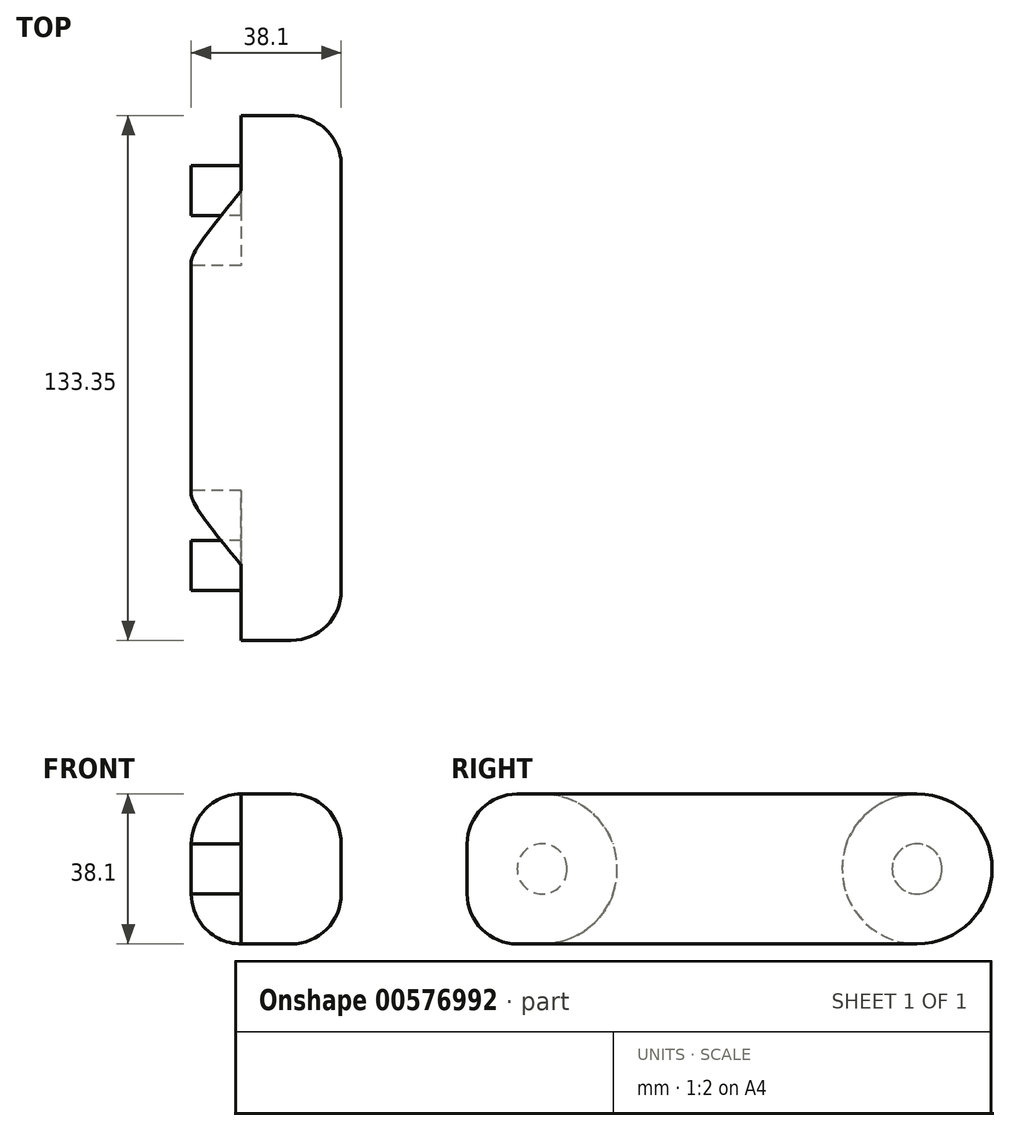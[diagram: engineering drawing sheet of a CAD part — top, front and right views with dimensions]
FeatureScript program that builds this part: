
annotation { "Feature Type Name" : "Feature", "Feature Type Description" : "" }
export const myFeature = defineFeature(function(context is Context, id is Id, definition is map)
    precondition{}
    {
        {
            var Q0;
            Q0=qCreatedBy(makeId("Right.planeOp"),FACE);
            var sketch = newSketch(context, id + "F0", { "sketchPlane" : qUnion([Q0])});
            skLineSegment(sketch, "E0.bottom", {"start": v(12.7, 0) * mm, "end": v(88.9, 0) * mm});
            skLineSegment(sketch, "E0.top", {"start": v(12.7, 38.1) * mm, "end": v(88.9, 38.1) * mm});
            skLineSegment(sketch, "E0.left", {"start": v(0, 12.7) * mm, "end": v(0, 25.4) * mm});
            skPoint(sketch, "E1.visualSharp", {"position": v(0, 38.1) * mm});
            skArc(sketch, "E1.filletArc", {"start": v(12.7, 38.1) * mm, "mid": v(3.72, 34.38) * mm, "end": v(0, 25.4) * mm});
            skPoint(sketch, "E2.visualSharp", {"position": v(101.6, 38.1) * mm});
            skPoint(sketch, "E3.visualSharp", {"position": v(101.6, 0) * mm});
            skPoint(sketch, "E4.visualSharp", {"position": v(0, 0) * mm});
            skArc(sketch, "E4.filletArc", {"start": v(0, 12.7) * mm, "mid": v(3.72, 3.72) * mm, "end": v(12.7, 0) * mm});
            skLineSegment(sketch, "E5", {"start": v(88.9, 0) * mm, "end": v(114.3, 0) * mm});
            skLineSegment(sketch, "E6", {"start": v(88.9, 38.1) * mm, "end": v(114.3, 38.1) * mm});
            skArc(sketch, "E7", {"start": v(114.3, 0) * mm, "mid": v(133.35, 19.05) * mm, "end": v(114.3, 38.1) * mm});
            skSolve(sketch);
        }
        {
            var Q0;
            Q0=makeQuery(id+"F0.imprint","IMPRINT",FACE,{"disambiguationData":[TD([[makeQuery(id+"F0.imprint","IMPRINT",EDGE,{"derivedFrom":sQuery(id+"F0.wireOp",EDGE,"E0.bottom")}),1.0]])]});
            extrude(context, id + "F1", {"entities" : qUnion([Q0]), "depth" : 38.1 * mm, "offsetDistance" : 25.4 * mm});
        }
        {
            var Q0;
            Q0=makeQuery(id+"F1.opExtrude","CAP_FACE",FACE,{"disambiguationData":[OSD([sQuery(id+"F0.wireOp",EDGE,"E0.bottom"),sQuery(id+"F0.wireOp",EDGE,"E0.top"),sQuery(id+"F0.wireOp",EDGE,"E0.left"),sQuery(id+"F0.wireOp",EDGE,"E1.filletArc"),sQuery(id+"F0.wireOp",EDGE,"E4.filletArc"),sQuery(id+"F0.wireOp",EDGE,"E5"),sQuery(id+"F0.wireOp",EDGE,"E6"),sQuery(id+"F0.wireOp",EDGE,"E7")])],"isStart":false});
            var Q1;
            Q1=makeQuery(id+"F1.opExtrude","CAP_FACE",FACE,{"disambiguationData":[OSD([sQuery(id+"F0.wireOp",EDGE,"E0.bottom"),sQuery(id+"F0.wireOp",EDGE,"E0.top"),sQuery(id+"F0.wireOp",EDGE,"E0.left"),sQuery(id+"F0.wireOp",EDGE,"E1.filletArc"),sQuery(id+"F0.wireOp",EDGE,"E4.filletArc"),sQuery(id+"F0.wireOp",EDGE,"E5"),sQuery(id+"F0.wireOp",EDGE,"E6"),sQuery(id+"F0.wireOp",EDGE,"E7")])],"isStart":true});
            fillet(context, id + "F2", {"entities" : qUnion([Q0, Q1]), "radius" : 12.7 * mm, "tangentPropagation" : true, "allowEdgeOverflow" : false});
        }
        {
            var Q0;
            Q0=makeQuery(id+"F1.opExtrude","CAP_FACE",FACE,{"disambiguationData":[OSD([sQuery(id+"F0.wireOp",EDGE,"E0.bottom"),sQuery(id+"F0.wireOp",EDGE,"E0.top"),sQuery(id+"F0.wireOp",EDGE,"E0.left"),sQuery(id+"F0.wireOp",EDGE,"E1.filletArc"),sQuery(id+"F0.wireOp",EDGE,"E4.filletArc"),sQuery(id+"F0.wireOp",EDGE,"E5"),sQuery(id+"F0.wireOp",EDGE,"E6"),sQuery(id+"F0.wireOp",EDGE,"E7")])],"isStart":true});
            var sketch = newSketch(context, id + "F3", { "sketchPlane" : qUnion([Q0])});
            skCircle(sketch, "E8", {"center": v(-114.3, 19.05) * mm, "radius": 6.35 * mm});
            skCircle(sketch, "E9", {"center": v(-114.3, 19.05) * mm, "radius": 19.05 * mm});
            skCircle(sketch, "E10", {"center": v(-19.05, 19.05) * mm, "radius": 6.35 * mm});
            skArc(sketch, "E11", {"start": v(-19.37, 38.1) * mm, "mid": v(-38.1, 18.89) * mm, "end": v(-19.05, 0) * mm});
            skLineSegment(sketch, "E12", {"start": v(-19.37, 38.1) * mm, "end": v(-15.41, 51.76) * mm});
            skLineSegment(sketch, "E13", {"start": v(-15.41, 51.76) * mm, "end": v(22.04, 45.63) * mm});
            skLineSegment(sketch, "E14", {"start": v(22.04, 45.63) * mm, "end": v(7.6, -14.7) * mm});
            skLineSegment(sketch, "E15", {"start": v(7.6, -14.7) * mm, "end": v(-15.28, -14.7) * mm});
            skLineSegment(sketch, "E16", {"start": v(-15.28, -14.7) * mm, "end": v(-19.05, 0) * mm});
            skSolve(sketch);
        }
        {
            var Q0;
            {var subQ0=sQuery(id+"F3.wireOp",EDGE,"E8");var subQ1=sQuery(id+"F0.wireOp",EDGE,"E6");var subQ2=sQuery(id+"F0.wireOp",EDGE,"E5");var subQ3=sQuery(id+"F0.wireOp",EDGE,"E0.top");var subQ4=sQuery(id+"F0.wireOp",EDGE,"E0.bottom");var subQ5=makeQuery(id+"F1.opExtrude","CAP_FACE",FACE,{"disambiguationData":[OSD([subQ4,subQ3,sQuery(id+"F0.wireOp",EDGE,"E0.left"),sQuery(id+"F0.wireOp",EDGE,"E1.filletArc"),sQuery(id+"F0.wireOp",EDGE,"E4.filletArc"),subQ2,subQ1,sQuery(id+"F0.wireOp",EDGE,"E7")])],"isStart":true});var subQ6=makeQuery(id+"F2.opFillet","BLEND_EDGE",EDGE,{"blendedFrom":[makeQuery(id+"F1.opExtrude","CAP_EDGE",EDGE,{"disambiguationData":[OSD([subQ4,subQ2])],"isStart":true}),subQ5],"blendedInto":[subQ5]});var subQ7=makeQuery(id+"F3.imprint","INTERSECT",VERTEX,{"derivedFrom":[subQ6,subQ0]});Q0=makeQuery(id+"F3.imprint","IMPRINT",FACE,{"disambiguationData":[TD([[makeQuery(id+"F3.imprint","IMPRINT",EDGE,{"disambiguationData":[TD([[subQ7,-1.0]])],"derivedFrom":subQ0}),-1.0]])]});}
            var Q1;
            {var subQ0=sQuery(id+"F3.wireOp",EDGE,"E8");var subQ1=sQuery(id+"F0.wireOp",EDGE,"E6");var subQ2=sQuery(id+"F0.wireOp",EDGE,"E5");var subQ3=sQuery(id+"F0.wireOp",EDGE,"E0.top");var subQ4=sQuery(id+"F0.wireOp",EDGE,"E0.bottom");var subQ5=makeQuery(id+"F1.opExtrude","CAP_FACE",FACE,{"disambiguationData":[OSD([subQ4,subQ3,sQuery(id+"F0.wireOp",EDGE,"E0.left"),sQuery(id+"F0.wireOp",EDGE,"E1.filletArc"),sQuery(id+"F0.wireOp",EDGE,"E4.filletArc"),subQ2,subQ1,sQuery(id+"F0.wireOp",EDGE,"E7")])],"isStart":true});var subQ6=makeQuery(id+"F2.opFillet","BLEND_EDGE",EDGE,{"blendedFrom":[makeQuery(id+"F1.opExtrude","CAP_EDGE",EDGE,{"disambiguationData":[OSD([subQ4,subQ2])],"isStart":true}),subQ5],"blendedInto":[subQ5]});var subQ7=makeQuery(id+"F3.imprint","INTERSECT",VERTEX,{"derivedFrom":[subQ6,subQ0]});Q1=makeQuery(id+"F3.imprint","IMPRINT",FACE,{"disambiguationData":[TD([[makeQuery(id+"F3.imprint","IMPRINT",EDGE,{"disambiguationData":[TD([[subQ7,1.0]])],"derivedFrom":subQ0}),-1.0]])]});}
            var Q2;
            {var subQ0=sQuery(id+"F3.wireOp",EDGE,"E10");var subQ1=sQuery(id+"F0.wireOp",EDGE,"E6");var subQ2=sQuery(id+"F0.wireOp",EDGE,"E5");var subQ3=sQuery(id+"F0.wireOp",EDGE,"E0.top");var subQ4=sQuery(id+"F0.wireOp",EDGE,"E0.bottom");var subQ5=makeQuery(id+"F1.opExtrude","CAP_FACE",FACE,{"disambiguationData":[OSD([subQ4,subQ3,sQuery(id+"F0.wireOp",EDGE,"E0.left"),sQuery(id+"F0.wireOp",EDGE,"E1.filletArc"),sQuery(id+"F0.wireOp",EDGE,"E4.filletArc"),subQ2,subQ1,sQuery(id+"F0.wireOp",EDGE,"E7")])],"isStart":true});var subQ6=makeQuery(id+"F2.opFillet","BLEND_EDGE",EDGE,{"blendedFrom":[makeQuery(id+"F1.opExtrude","CAP_EDGE",EDGE,{"disambiguationData":[OSD([subQ3,subQ1])],"isStart":true}),subQ5],"blendedInto":[subQ5]});var subQ7=makeQuery(id+"F3.imprint","INTERSECT",VERTEX,{"derivedFrom":[subQ6,subQ0]});Q2=makeQuery(id+"F3.imprint","IMPRINT",FACE,{"disambiguationData":[TD([[makeQuery(id+"F3.imprint","IMPRINT",EDGE,{"disambiguationData":[TD([[subQ7,-1.0]])],"derivedFrom":subQ0}),-1.0]])]});}
            var Q3;
            {var subQ1=sQuery(id+"F0.wireOp",EDGE,"E6");var subQ2=sQuery(id+"F0.wireOp",EDGE,"E5");var subQ3=sQuery(id+"F0.wireOp",EDGE,"E0.left");var subQ4=sQuery(id+"F0.wireOp",EDGE,"E0.top");var subQ5=sQuery(id+"F0.wireOp",EDGE,"E0.bottom");var subQ6=makeQuery(id+"F1.opExtrude","CAP_FACE",FACE,{"disambiguationData":[OSD([subQ5,subQ4,subQ3,sQuery(id+"F0.wireOp",EDGE,"E1.filletArc"),sQuery(id+"F0.wireOp",EDGE,"E4.filletArc"),subQ2,subQ1,sQuery(id+"F0.wireOp",EDGE,"E7")])],"isStart":true});var subQ7=makeQuery(id+"F2.opFillet","BLEND_EDGE",EDGE,{"blendedFrom":[makeQuery(id+"F1.opExtrude","CAP_EDGE",EDGE,{"disambiguationData":[OSD([subQ5,subQ2])],"isStart":true}),subQ6],"blendedInto":[subQ6]});var subQ9=sQuery(id+"F3.wireOp",EDGE,"E11");var subQ10=makeQuery(id+"F3.imprint","INTERSECT",VERTEX,{"derivedFrom":[subQ7,subQ9]});Q3=makeQuery(id+"F3.imprint","IMPRINT",FACE,{"disambiguationData":[TD([[makeQuery(id+"F3.imprint","IMPRINT",EDGE,{"disambiguationData":[TD([[subQ10,-1.0]])],"derivedFrom":subQ9}),1.0]])]});}
            var Q4;
            {var subQ0=sQuery(id+"F3.wireOp",EDGE,"E10");var subQ1=sQuery(id+"F0.wireOp",EDGE,"E6");var subQ2=sQuery(id+"F0.wireOp",EDGE,"E0.left");var subQ3=sQuery(id+"F0.wireOp",EDGE,"E0.top");var subQ4=makeQuery(id+"F1.opExtrude","CAP_FACE",FACE,{"disambiguationData":[OSD([sQuery(id+"F0.wireOp",EDGE,"E0.bottom"),subQ3,subQ2,sQuery(id+"F0.wireOp",EDGE,"E1.filletArc"),sQuery(id+"F0.wireOp",EDGE,"E4.filletArc"),sQuery(id+"F0.wireOp",EDGE,"E5"),subQ1,sQuery(id+"F0.wireOp",EDGE,"E7")])],"isStart":true});var subQ7=makeQuery(id+"F2.opFillet","BLEND_EDGE",EDGE,{"blendedFrom":[makeQuery(id+"F1.opExtrude","CAP_EDGE",EDGE,{"disambiguationData":[OSD([subQ2])],"isStart":true}),subQ4],"blendedInto":[subQ4]});var subQ8=makeQuery(id+"F3.imprint","INTERSECT",VERTEX,{"derivedFrom":[subQ7,subQ0]});Q4=makeQuery(id+"F3.imprint","IMPRINT",FACE,{"disambiguationData":[TD([[makeQuery(id+"F3.imprint","IMPRINT",EDGE,{"disambiguationData":[TD([[subQ8,-1.0]])],"derivedFrom":subQ0}),-1.0]])]});}
            var Q5;
            {var subQ0=sQuery(id+"F3.wireOp",EDGE,"E10");var subQ1=sQuery(id+"F0.wireOp",EDGE,"E5");var subQ2=sQuery(id+"F0.wireOp",EDGE,"E0.left");var subQ3=sQuery(id+"F0.wireOp",EDGE,"E0.bottom");var subQ4=makeQuery(id+"F1.opExtrude","CAP_FACE",FACE,{"disambiguationData":[OSD([subQ3,sQuery(id+"F0.wireOp",EDGE,"E0.top"),subQ2,sQuery(id+"F0.wireOp",EDGE,"E1.filletArc"),sQuery(id+"F0.wireOp",EDGE,"E4.filletArc"),subQ1,sQuery(id+"F0.wireOp",EDGE,"E6"),sQuery(id+"F0.wireOp",EDGE,"E7")])],"isStart":true});var subQ5=makeQuery(id+"F2.opFillet","BLEND_EDGE",EDGE,{"blendedFrom":[makeQuery(id+"F1.opExtrude","CAP_EDGE",EDGE,{"disambiguationData":[OSD([subQ2])],"isStart":true}),subQ4],"blendedInto":[subQ4]});var subQ6=makeQuery(id+"F3.imprint","INTERSECT",VERTEX,{"derivedFrom":[subQ5,subQ0]});Q5=makeQuery(id+"F3.imprint","IMPRINT",FACE,{"disambiguationData":[TD([[makeQuery(id+"F3.imprint","IMPRINT",EDGE,{"disambiguationData":[TD([[subQ6,1.0]])],"derivedFrom":subQ0}),-1.0]])]});}
            extrude(context, id + "F4", {"entities" : qUnion([Q0, Q1, Q2, Q3, Q4, Q5]), "operationType" : NewBodyOperationType.REMOVE, "oppositeDirection" : true, "depth" : 12.7 * mm, "offsetDistance" : 25.4 * mm});
        }
    });
